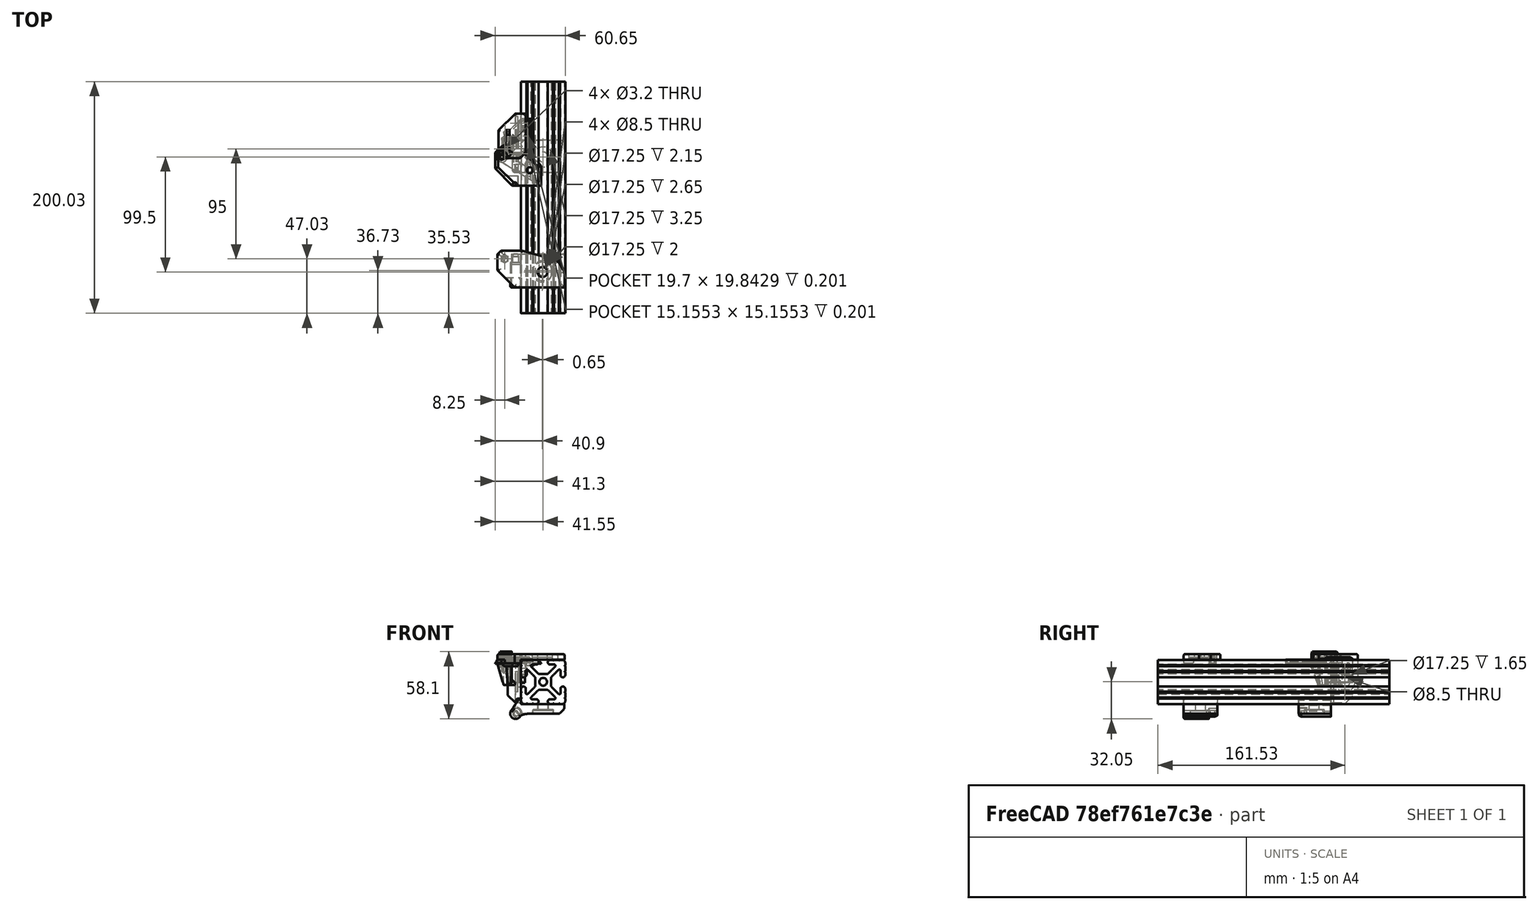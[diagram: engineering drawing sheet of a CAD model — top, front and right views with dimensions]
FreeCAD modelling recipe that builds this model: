
FCSTD DOCUMENT  (FreeCAD 0.18R)
Label: rambo-mounts
License: All rights reserved
LicenseURL: http://en.wikipedia.org/wiki/All_rights_reserved
objects: Sketcher::SketchObject×24, PartDesign::Fillet×15, PartDesign::Pad×11, PartDesign::Pocket×11, Part::Feature×6, PartDesign::Body×4, Mesh::Feature×2, PartDesign::Revolution×2, PartDesign::Chamfer×1
note: 98 computed .brp shape members not serialized (recipe doc carries the construction recipe); baked Part::Feature solids carry a one-line shape summary decoded from their .brp

FEATURE [Sketcher::SketchObject] Sketch
  MapMode = 5
  Support = -> [XY_Plane]
  sketch-geometry (7):
    g0: LineSegment StartX=-3 StartY=23 StartZ=0 EndX=-3 EndY=4.25 EndZ=0
    g1: LineSegment StartX=-3 StartY=4.25 StartZ=0 EndX=2.25 EndY=-1 EndZ=0
    g2: LineSegment StartX=2.25 StartY=-1 StartZ=0 EndX=15.7 EndY=-1 EndZ=0
    g3: LineSegment StartX=15.7 StartY=-1 StartZ=0 EndX=20.5 EndY=3.8 EndZ=0
    g4: LineSegment StartX=20.5 StartY=37.5 StartZ=0 EndX=20.5 EndY=3.8 EndZ=0
    g5: LineSegment StartX=11.5 StartY=37.5 StartZ=0 EndX=20.5 EndY=37.5 EndZ=0
    g6: LineSegment StartX=11.5 StartY=37.5 StartZ=0 EndX=-3 EndY=23 EndZ=0
  constraints (21):
    c: Coincident(g1,g0)
    c: Coincident(g2,g1)
    c: Horizontal(g2)
    c: Coincident(g4,g3)
    c: Vertical(g4)
    c: Coincident(g5,g4)
    c: Horizontal(g5)
    c: Coincident(g6,g5)
    c: Coincident(g6,g0)
    c: Angle(g1,g0) = 2.35619
    c: Angle(g0,g6) = 2.35619
    c: Angle(g3,g2) = 2.35619
    c: DistanceX(g-1,g5) = 11.5
    c: DistanceY(g-1,g5) = 37.5
    c: DistanceX(g5,g5) = 9
    c: Coincident(g3,g2)
    c: DistanceX(g-1,g2) = 15.7
    c: DistanceX(g-1,g1) = 2.25
    c: Vertical(g0)
    c: DistanceX(g0,g-1) = 3
    c: DistanceY(g1,g-1) = 1
FEATURE [Part::Feature] rambo_base_upper_mount
  shape: bbox 25.4 x 33.05 x 22.5 mm, 98 faces (baked)
  expr: Placement.Base.z = 0
FEATURE [Part::Feature] rambo_base_lower_mount
  shape: bbox 39.91 x 31.71 x 6.307 mm, 79 faces (baked)
FEATURE [Part::Feature] rambo_lid_lower_hinge
  shape: bbox 15.91 x 28.51 x 29.3 mm, 59 faces (baked)
FEATURE [Part::Feature] rambo_base_upper_mount_cs
  shape: bbox 20 x 29.18 x 3e-07 mm, 0 faces, 0 solids (baked)
FEATURE [PartDesign::Pad] Pad
  Length = 5
  Length2 = 100
  Profile = -> Sketch
  Type = 0
FEATURE [Sketcher::SketchObject] Sketch001
  AttachmentOffset = pos=(0,0,-14.5) rot=(0,0,1;0rad)
  MapMode = 5
  Placement = pos=(0,14.5,3.2e-15) rot=(1,0,0;1.5708rad)
  Support = -> [XZ_Plane]
  sketch-geometry (5):
    g0: LineSegment StartX=5 StartY=0 StartZ=0 EndX=5 EndY=-30.5 EndZ=0
    g1: LineSegment StartX=5 StartY=-30.5 StartZ=0 EndX=11.5 EndY=-37 EndZ=0
    g2: LineSegment StartX=11.5 StartY=-37 StartZ=0 EndX=16.5 EndY=-37 EndZ=0
    g3: LineSegment StartX=16.5 StartY=-37 StartZ=0 EndX=16.5 EndY=0 EndZ=0
    g4: LineSegment StartX=16.5 StartY=0 StartZ=0 EndX=5 EndY=0 EndZ=0
  constraints (15):
    c: Horizontal(g2)
    c: PointOnObject(g3,g-1)
    c: Vertical(g3)
    c: Angle(g1,g0) = 2.35619
    c: Coincident(g1,g2)
    c: Coincident(g0,g1)
    c: Coincident(g3,g2)
    c: Coincident(g4,g3)
    c: Vertical(g0)
    c: Coincident(g4,g0)
    c: Horizontal(g4)
    c: DistanceX(g-1,g0) = 5
    c: DistanceX(g-1,g3) = 16.5
    c: DistanceY(g2,g-1) = 37
    c: DistanceX(g2,g2) = 5
FEATURE [PartDesign::Pad] Pad001
  BaseFeature = -> Pad
  Length = 2
  Length2 = 100
  Profile = -> Sketch001
  Reversed = true
  Type = 0
FEATURE [Sketcher::SketchObject] Sketch002
  AttachmentOffset = pos=(0,0,16.5) rot=(0,0,1;0rad)
  MapMode = 5
  Placement = pos=(16.5,-3.7e-15,3.7e-15) rot=(0.57735,0.57735,0.57735;2.0944rad)
  Support = -> [YZ_Plane]
  sketch-geometry (6):
    g0: LineSegment StartX=16.5 StartY=0 StartZ=0 EndX=37.5 EndY=0 EndZ=0
    g1: LineSegment StartX=16.5 StartY=0 StartZ=0 EndX=16.5 EndY=-37 EndZ=0
    g2: LineSegment StartX=16.5 StartY=-37 StartZ=0 EndX=27.5 EndY=-37 EndZ=0
    g3: LineSegment StartX=37.5 StartY=0 StartZ=0 EndX=37.5 EndY=-27 EndZ=0
    g4: Circle CenterX=26.5 CenterY=-19.05 CenterZ=0 NormalX=0 NormalY=0 NormalZ=1 AngleXU=0 Radius=4.25
    g5: LineSegment StartX=27.5 StartY=-37 StartZ=0 EndX=37.5 EndY=-27 EndZ=0
  constraints (18):
    c: Coincident(g1,g0)
    c: Vertical(g1)
    c: Horizontal(g2)
    c: DistanceX(g-1,g0) = 16.5
    c: DistanceY(g2,g-1) = 37
    c: Coincident(g2,g1)
    c: Vertical(g3)
    c: Diameter(g4) = 8.5
    c: DistanceY(g4,g-1) = 19.05
    c: Horizontal(g0)
    c: DistanceY(g-1,g0) = 0
    c: DistanceX(g0,g4) = 10
    c: DistanceX(g0,g3) = 21
    c: Coincident(g5,g2)
    c: DistanceX(g2,g5) = 10
    c: Coincident(g5,g3)
    c: Angle(g3,g5) = 2.35619
    c: Coincident(g3,g0)
FEATURE [PartDesign::Pad] Pad002
  BaseFeature = -> Pad001
  Length = 5
  Length2 = 100
  Profile = -> Sketch002
  Reversed = true
  Type = 0
FEATURE [Sketcher::SketchObject] Sketch003
  AttachmentOffset = pos=(0,0,11.5) rot=(0,0,1;0rad)
  MapMode = 5
  Placement = pos=(11.5,-2.6e-15,2.6e-15) rot=(0.57735,0.57735,0.57735;2.0944rad)
  Support = -> [YZ_Plane]
  sketch-geometry (1):
    g0: Circle CenterX=26.5 CenterY=-19.05 CenterZ=0 NormalX=0 NormalY=0 NormalZ=1 AngleXU=0 Radius=8.625
  constraints (3):
    c: Diameter(g0) = 17.25
    c: DistanceY(g0,g-1) = 19.05
    c: DistanceX(g-1,g0) = 26.5
FEATURE [PartDesign::Pocket] Pocket
  BaseFeature = -> Pad002
  Length = 2
  Length2 = 100
  Profile = -> Sketch003
  Reversed = true
  Type = 0
FEATURE [Sketcher::SketchObject] Sketch004
  AttachmentOffset = pos=(2.25,7,0) rot=(0,0,1;0rad)
  MapMode = 5
  Placement = pos=(2.25,7,0) rot=(0,0,1;0rad)
  Support = -> [XY_Plane]
  sketch-geometry (8):
    g0: LineSegment StartX=0 StartY=-3.15 StartZ=0 EndX=2.72798 EndY=-1.575 EndZ=0
    g1: LineSegment StartX=2.72798 StartY=-1.575 StartZ=0 EndX=2.72798 EndY=1.575 EndZ=0
    g2: LineSegment StartX=2.72798 StartY=1.575 StartZ=0 EndX=0 EndY=3.15 EndZ=0
    g3: LineSegment StartX=0 StartY=3.15 StartZ=0 EndX=-2.72798 EndY=1.575 EndZ=0
    g4: LineSegment StartX=-2.72798 StartY=1.575 StartZ=0 EndX=-2.72798 EndY=-1.575 EndZ=0
    g5: LineSegment StartX=-2.72798 StartY=-1.575 StartZ=0 EndX=0 EndY=-3.15 EndZ=0
    g6: Circle [constr] CenterX=0 CenterY=0 CenterZ=0 NormalX=0 NormalY=0 NormalZ=1 AngleXU=0 Radius=3.15
    g7: Circle CenterX=0 CenterY=0 CenterZ=0 NormalX=0 NormalY=0 NormalZ=1 AngleXU=0 Radius=1.6
  constraints (18):
    c: Coincident(g0,g1)
    c: Coincident(g1,g2)
    c: Coincident(g2,g3)
    c: Coincident(g3,g4)
    c: Coincident(g4,g5)
    c: Coincident(g5,g0)
    c: Equal(g0, g1-g5) x5
    c: PointOnObject(g0,g6)
    c: PointOnObject(g1,g6)
    c: PointOnObject(g2,g6)
    c: PointOnObject(g3,g6)
    c: PointOnObject(g4,g6)
    c: PointOnObject(g5,g6)
    c: Vertical(g1)
    c: Coincident(g6,g-1)
    c: DistanceY(g-1,g2) = 3.15
    c: Coincident(g7,g-1)
    c: Diameter(g7) = 3.2
FEATURE [PartDesign::Pad] Pad003
  BaseFeature = -> Pocket
  Length = 3
  Length2 = 100
  Profile = -> Sketch004
  Reversed = true
  Type = 0
FEATURE [Sketcher::SketchObject] Sketch005
  AttachmentOffset = pos=(0,0,-3) rot=(0,0,1;0rad)
  MapMode = 5
  Placement = pos=(0,0,-3) rot=(0,0,1;0rad)
  Support = -> [XY_Plane]
  sketch-geometry (1):
    g0: Circle CenterX=2.25 CenterY=7 CenterZ=0 NormalX=0 NormalY=0 NormalZ=1 AngleXU=0 Radius=1.6
  constraints (3):
    c: Diameter(g0) = 3.2
    c: DistanceX(g-1,g0) = 2.25
    c: DistanceY(g-1,g0) = 7
FEATURE [PartDesign::Pocket] Pocket001
  BaseFeature = -> Pad003
  Length = 5
  Length2 = 100
  Profile = -> Sketch005
  Reversed = true
  Type = 1
FEATURE [Part::Feature] _515_extrusion_200_25mm_7_7_8in
  Placement = pos=(-110.45,65,-76.25) rot=(1,0,0;1.5708rad)
  shape: bbox 38.1 x 200 x 38.1 mm, 113 faces (baked)
FEATURE [Mesh::Feature] Einsy_base  label="Einsy-base"
  Placement = pos=(16.25,14.5,0) rot=(-0.707107,0.707107,0;3.14159rad)
FEATURE [Part::Feature] rambo_lower_mount
  Placement = pos=(2.25,-88,0) rot=(0,0,1;0rad)
  shape: bbox 58.05 x 31.7 x 8 mm, 46 faces (baked)
FEATURE [Mesh::Feature] Einsy_doors  label="Einsy-doors"
  Placement = pos=(-75.75,14.5,-51) rot=(0,0,1;4.71239rad)
FEATURE [Sketcher::SketchObject] Sketch006
  MapMode = 5
  Support = -> [XY_Plane001]
  sketch-geometry (10):
    g0: LineSegment StartX=0.5 StartY=0.25 StartZ=0 EndX=37.5 EndY=0.25 EndZ=0
    g1: LineSegment StartX=37.5 StartY=0.25 StartZ=0 EndX=37.5 EndY=4.25 EndZ=0
    g2: LineSegment StartX=33.5 StartY=8.5 StartZ=0 EndX=37.5 EndY=4.25 EndZ=0
    g3: LineSegment StartX=-8.36135 StartY=6 StartZ=0 EndX=-1.5 EndY=-4.23326 EndZ=0
    g4: LineSegment StartX=-1 StartY=-4.5 StartZ=0 EndX=0.25 EndY=-4.5 EndZ=0
    g5: LineSegment StartX=33.5 StartY=8.5 StartZ=0 EndX=0.1 EndY=8.5 EndZ=0
    g6: LineSegment StartX=0.25 StartY=-4.5 StartZ=0 EndX=0.25 EndY=0 EndZ=0
    g7: ArcOfCircle CenterX=0.5 CenterY=0 CenterZ=0 NormalX=0 NormalY=0 NormalZ=1 AngleXU=0 Radius=0.25 StartAngle=1.5708 EndAngle=3.14159
    g8: ArcOfCircle CenterX=-4.5 CenterY=8.5 CenterZ=0 NormalX=0 NormalY=0 NormalZ=1 AngleXU=0 Radius=4.6 StartAngle=3.71617 EndAngle=6.28319
    g9: ArcOfCircle CenterX=-1 CenterY=-3.89801 CenterZ=0 NormalX=0 NormalY=0 NormalZ=1 AngleXU=0 Radius=0.601989 StartAngle=3.73224 EndAngle=4.71239
  constraints (29):
    c: Horizontal(g0)
    c: Coincident(g1,g0)
    c: Vertical(g1)
    c: DistanceY(g0,g1) = 4
    c: Coincident(g2,g1)
    c: Horizontal(g5)
    c: Coincident(g5,g2)
    c: DistanceX(g2,g1) = 4
    c: Horizontal(g4)
    c: DistanceX(g-1,g4) = 0.25
    c: Coincident(g6,g4)
    c: Vertical(g6)
    c: Tangent(g0,g7) = 1.5708
    c: Tangent(g6,g7) = 1.5708
    c: DistanceX(g6,g7) = 0.25
    c: PointOnObject(g7,g-1)
    c: Diameter(g8) = 9.2
    c: DistanceX(g8,g-1) = 4.5
    c: DistanceY(g-1,g8) = 8.5
    c: DistanceX(g0,g0) = 37
    c: DistanceY(g6,g6) = 4.5
    c: Tangent(g3,g9) = -1.5708
    c: Tangent(g4,g9) = -1.5708
    c: DistanceX(g3,g9) = 0.5
    c: DistanceX(g4,g4) = 1.25
    c: Coincident(g8,g3)
    c: Coincident(g8,g5)
    c: DistanceY(g-1,g3) = 6
    c: DistanceY(g-1,g5) = 8.5
FEATURE [PartDesign::Pad] Pad004
  Length = 29
  Length2 = 100
  Profile = -> Sketch006
  Reversed = true
  Type = 0
FEATURE [Sketcher::SketchObject] Sketch007
  AttachmentOffset = pos=(-4.5,-9.3,-8.49) rot=(0,1,0;-4.71239rad)
  MapMode = 5
  Placement = pos=(-4.5,8.49,-9.3) rot=(0.57735,0.57735,0.57735;2.0944rad)
  Support = -> [XZ_Plane001]
  sketch-geometry (8):
    g0: LineSegment StartX=-1.75 StartY=9.3 StartZ=0 EndX=0 EndY=9.3 EndZ=0
    g1: LineSegment StartX=-1.75 StartY=9.3 StartZ=0 EndX=-2.5 EndY=7.15 EndZ=0
    g2: LineSegment StartX=-2.5 StartY=7.15 StartZ=0 EndX=-2.5 EndY=2 EndZ=0
    g3: LineSegment StartX=0 StartY=0 StartZ=0 EndX=0 EndY=9.3 EndZ=0
    g4: LineSegment StartX=-2.5 StartY=2 StartZ=0 EndX=-4.6 EndY=2 EndZ=0
    g5: LineSegment StartX=-4.6 StartY=2 StartZ=0 EndX=-4.6 EndY=0 EndZ=0
    g6: LineSegment StartX=-4.6 StartY=0 StartZ=0 EndX=0 EndY=0 EndZ=0
    g7: LineSegment StartX=0 StartY=9.3 StartZ=0 EndX=0 EndY=0 EndZ=0
  constraints (23):
    c: Horizontal(g0)
    c: Coincident(g2,g1)
    c: Vertical(g2)
    c: Coincident(g3,g0)
    c: Vertical(g3)
    c: Coincident(g0,g1)
    c: DistanceX(g0,g0) = 1.75
    c: PointOnObject(g3,g-2)
    c: DistanceX(g1,g3) = 2.5
    c: DistanceY(g1,g0) = 2.15
    c: DistanceY(g2,g1) = 5.15
    c: Coincident(g4,g2)
    c: Horizontal(g4)
    c: DistanceX(g4,g2) = 2.1
    c: Coincident(g5,g4)
    c: PointOnObject(g5,g-1)
    c: Vertical(g5)
    c: Coincident(g6,g5)
    c: Horizontal(g6)
    c: DistanceY(g5,g4) = 2
    c: Coincident(g7,g0)
    c: Coincident(g7,g6)
    c: Coincident(g3,g6)
FEATURE [PartDesign::Revolution] Revolution
  Angle = 360
  Axis = (0,-2e-16,1)
  Base = (-4.5,8.49,-9.3)
  BaseFeature = -> Pad004
  Midplane = true
  Profile = -> Sketch007
  ReferenceAxis = -> Sketch007 [V_Axis]
  Refine = true
FEATURE [Sketcher::SketchObject] Sketch008
  AttachmentOffset = pos=(0,0,-29) rot=(0,0,1;0rad)
  MapMode = 5
  Placement = pos=(0,0,-29) rot=(0,0,1;0rad)
  Support = -> [XY_Plane001]
  sketch-geometry (1):
    g0: Circle CenterX=-4.5 CenterY=8.5 CenterZ=0 NormalX=0 NormalY=0 NormalZ=1 AngleXU=0 Radius=4.6
  constraints (3):
    c: Diameter(g0) = 9.2
    c: DistanceX(g0,g-1) = 4.5
    c: DistanceY(g-1,g0) = 8.5
FEATURE [PartDesign::Pad] Pad005
  BaseFeature = -> Revolution
  Length = 19.7
  Length2 = 100
  Profile = -> Sketch008
  Type = 0
FEATURE [Sketcher::SketchObject] Sketch009
  MapMode = 5
  Support = -> [XY_Plane001]
  sketch-geometry (9):
    g0: ArcOfCircle CenterX=-4.5 CenterY=8.5 CenterZ=0 NormalX=0 NormalY=0 NormalZ=1 AngleXU=0 Radius=4.6 StartAngle=0 EndAngle=0.511093
    g1: Circle [constr] CenterX=-0.487831 CenterY=10.75 CenterZ=0 NormalX=0 NormalY=0 NormalZ=1 AngleXU=0 Radius=0.8
    g2: Circle [constr] CenterX=1.778 CenterY=8.5 CenterZ=0 NormalX=0 NormalY=0 NormalZ=1 AngleXU=0 Radius=0.8
    g3: Circle [constr] CenterX=9.875 CenterY=8.5 CenterZ=0 NormalX=0 NormalY=0 NormalZ=1 AngleXU=0 Radius=0.8
    g4: BSplineCurve PolesCount=3 KnotsCount=2 Degree=2 IsPeriodic=0
    g5: GeomPoint [constr] X=-0.487831 Y=10.75 Z=0
    g6: GeomPoint [constr] X=9.875 Y=8.5 Z=0
    g7: LineSegment StartX=0.1 StartY=8.5 StartZ=0 EndX=1.778 EndY=8.5 EndZ=0
    g8: LineSegment StartX=1.778 StartY=8.5 StartZ=0 EndX=9.875 EndY=8.5 EndZ=0
  constraints (21):
    c: Diameter(g0) = 9.2
    c: DistanceX(g0,g-1) = 4.5
    c: DistanceY(g-1,g0) = 8.5
    c: Radius(g1) = 0.8
    c: Equal(g1,g2)
    c: Equal(g1,g3)
    c: InternalAlignment(g1,g4)
    c: InternalAlignment(g2,g4)
    c: InternalAlignment(g3,g4)
    c: InternalAlignment(g5,g4)
    c: InternalAlignment(g6,g4)
    c: DistanceX(g-1,g4) = 9.875
    c: DistanceY(g4,g2) = 0
    c: Horizontal(g7)
    c: Coincident(g7,g2)
    c: Coincident(g0,g7)
    c: Coincident(g0,g4)
    c: DistanceY(g-1,g4) = 8.5
    c: DistanceY(g0,g0) = 2.25
    c: Coincident(g8,g4)
    c: Horizontal(g8)
FEATURE [PartDesign::Pad] Pad006
  BaseFeature = -> Pad005
  Length = 29
  Length2 = 100
  Profile = -> Sketch009
  Reversed = true
  Type = 0
FEATURE [Sketcher::SketchObject] Sketch010
  MapMode = 5
  Placement = pos=(0,0,0) rot=(1,0,0;1.5708rad)
  Support = -> [XZ_Plane001]
  sketch-geometry (1):
    g0: Circle CenterX=19.05 CenterY=-14.5 CenterZ=0 NormalX=0 NormalY=0 NormalZ=1 AngleXU=0 Radius=4.25
  constraints (3):
    c: Diameter(g0) = 8.5
    c: DistanceX(g-1,g0) = 19.05
    c: DistanceY(g0,g-1) = 14.5
FEATURE [PartDesign::Pocket] Pocket002
  BaseFeature = -> Pad006
  Length = 5
  Length2 = 100
  Profile = -> Sketch010
  Type = 1
FEATURE [Sketcher::SketchObject] Sketch011
  AttachmentOffset = pos=(0,0,-6) rot=(0,0,1;0rad)
  MapMode = 5
  Placement = pos=(0,6,1.3e-15) rot=(1,0,0;1.5708rad)
  Support = -> [XZ_Plane001]
  sketch-geometry (1):
    g0: Circle CenterX=19.05 CenterY=-14.5 CenterZ=0 NormalX=0 NormalY=0 NormalZ=1 AngleXU=0 Radius=8.625
  constraints (3):
    c: Diameter(g0) = 17.25
    c: DistanceX(g-1,g0) = 19.05
    c: DistanceY(g0,g-1) = 14.5
FEATURE [PartDesign::Pocket] Pocket003
  BaseFeature = -> Pocket002
  Length = 5
  Length2 = 100
  Profile = -> Sketch011
  Type = 0
FEATURE [PartDesign::Fillet] Fillet005
  Base = -> Pocket003 [Edge33,Edge58,Edge28,Edge52,Edge27,Edge26,Edge51,Edge15,Edge14,Edge16,Edge56]
  BaseFeature = -> Pocket003
  Radius = 1.3
FEATURE [PartDesign::Fillet] Fillet006
  Base = -> Fillet005 [Edge109]
  BaseFeature = -> Fillet005
  Radius = 0.35
FEATURE [PartDesign::Body] Body001  label="rambo-lower-hinge"
  Group = -> [Sketch006,Pad004,Sketch007,Revolution,Sketch008,Pad005,Sketch009,Pad006,Sketch010,Pocket002,Sketch011,Pocket003,Fillet005,Fillet006]
  Origin = -> Origin001
  Placement = pos=(16.25,-83.8,-38) rot=(-1,0,0;1.5708rad)
  Tip = -> Fillet006
FEATURE [Sketcher::SketchObject] Sketch012
  AttachmentOffset = pos=(16,14.5,-38.1) rot=(1,0,0;-1.5708rad)
  MapMode = 5
  Placement = pos=(16,14.5,-38.1) rot=(1,0,0;4.71239rad)
  Support = -> [XY_Plane002]
  sketch-geometry (11):
    g0: LineSegment StartX=0.5 StartY=0.25 StartZ=0 EndX=37.5 EndY=0.25 EndZ=0
    g1: LineSegment StartX=37.5 StartY=0.25 StartZ=0 EndX=37.5 EndY=4.25 EndZ=0
    g2: LineSegment StartX=33.5 StartY=8.5 StartZ=0 EndX=37.5 EndY=4.25 EndZ=0
    g3: LineSegment StartX=-2.71273 StartY=-4.5 StartZ=0 EndX=0.25 EndY=-4.5 EndZ=0
    g4: LineSegment StartX=33.5 StartY=8.5 StartZ=0 EndX=-1.752 EndY=8.5 EndZ=0
    g5: LineSegment StartX=0.25 StartY=-4.5 StartZ=0 EndX=0.25 EndY=0 EndZ=0
    g6: ArcOfCircle CenterX=0.5 CenterY=0 CenterZ=0 NormalX=0 NormalY=0 NormalZ=1 AngleXU=0 Radius=0.25 StartAngle=1.5708 EndAngle=3.14159
    g7: LineSegment StartX=-5.87481 StartY=6.5 StartZ=0 EndX=-4.064 EndY=1.4 EndZ=0
    g8: LineSegment StartX=-4.064 StartY=1.4 StartZ=0 EndX=-4.064 EndY=-3.14873 EndZ=0
    g9: LineSegment StartX=-4.064 StartY=-3.14873 StartZ=0 EndX=-2.71273 EndY=-4.5 EndZ=0
    g10: ArcOfCircle CenterX=-4.25 CenterY=8.4 CenterZ=0 NormalX=0 NormalY=0 NormalZ=1 AngleXU=0 Radius=2.5 StartAngle=0.0400107 EndAngle=4.00491
  constraints (28):
    c: Horizontal(g0)
    c: Coincident(g1,g0)
    c: Vertical(g1)
    c: DistanceY(g0,g1) = 4
    c: Coincident(g2,g1)
    c: Horizontal(g4)
    c: Coincident(g4,g2)
    c: DistanceX(g2,g1) = 4
    c: Horizontal(g3)
    c: Coincident(g5,g3)
    c: Vertical(g5)
    c: Tangent(g0,g6) = 1.5708
    c: Tangent(g5,g6) = 1.5708
    c: DistanceX(g5,g6) = 0.25
    c: PointOnObject(g6,g-1)
    c: DistanceX(g0,g0) = 37
    c: DistanceY(g5,g5) = 4.5
    c: Vertical(g8)
    c: Coincident(g9,g3)
    c: Coincident(g9,g8)
    c: Coincident(g8,g7)
    c: Angle(g9,g8) = 2.35619
    c: Diameter(g10) = 5
    c: DistanceX(g10,g-1) = 4.25
    c: DistanceY(g-1,g10) = 8.4
    c: DistanceY(g-1,g7) = 1.4
    c: Coincident(g10,g4)
    c: Coincident(g10,g7)
FEATURE [PartDesign::Pad] Pad007
  Length = 28
  Length2 = 100
  Profile = -> Sketch012
  Reversed = true
  Type = 0
FEATURE [Sketcher::SketchObject] Sketch013
  AttachmentOffset = pos=(0,0,6.5) rot=(0,0,1;0rad)
  MapMode = 5
  Placement = pos=(0,-6.5,-1.4e-15) rot=(1,0,0;1.5708rad)
  Support = -> [XZ_Plane002]
  sketch-geometry (1):
    g0: Circle CenterX=11.75 CenterY=-46.5 CenterZ=0 NormalX=0 NormalY=0 NormalZ=1 AngleXU=0 Radius=4.625
  constraints (3):
    c: Diameter(g0) = 9.25
    c: DistanceX(g-1,g0) = 11.75
    c: DistanceY(g0,g-1) = 46.5
FEATURE [PartDesign::Pocket] Pocket004
  BaseFeature = -> Pad007
  Length = 7
  Length2 = 100
  Profile = -> Sketch013
  Reversed = true
  Type = 0
FEATURE [Sketcher::SketchObject] Sketch014
  AttachmentOffset = pos=(-6.5,-46.5,11.75) rot=(0,0,1;0rad)
  MapMode = 5
  Placement = pos=(11.75,-6.5,-46.5) rot=(0.57735,0.57735,0.57735;2.0944rad)
  Support = -> [YZ_Plane002]
  sketch-geometry (5):
    g0: LineSegment StartX=-6.73205 StartY=1.5 StartZ=0 EndX=-6.73205 EndY=0 EndZ=0
    g1: LineSegment StartX=-5 StartY=2.5 StartZ=0 EndX=0 EndY=2.5 EndZ=0
    g2: LineSegment StartX=0 StartY=2.5 StartZ=0 EndX=0 EndY=0 EndZ=0
    g3: LineSegment StartX=-6.73205 StartY=0 StartZ=0 EndX=0 EndY=0 EndZ=0
    g4: LineSegment StartX=-6.73205 StartY=1.5 StartZ=0 EndX=-5 EndY=2.5 EndZ=0
  constraints (14):
    c: Vertical(g0)
    c: Horizontal(g1)
    c: Coincident(g2,g1)
    c: Vertical(g2)
    c: Coincident(g3,g2)
    c: Horizontal(g3)
    c: Coincident(g0,g3)
    c: DistanceY(g2,g2) = 2.5
    c: Coincident(g4,g0)
    c: Coincident(g4,g1)
    c: DistanceY(g0,g0) = 1.5
    c: DistanceX(g1,g1) = 5
    c: Angle(g0,g4) = 2.0944
    c: Coincident(g2,g-1)
FEATURE [PartDesign::Revolution] Revolution001
  Angle = 360
  Axis = (3e-16,1,-2e-16)
  Base = (11.75,-6.5,-46.5)
  BaseFeature = -> Pocket004
  Profile = -> Sketch014
  ReferenceAxis = -> Sketch014 [H_Axis]
FEATURE [Sketcher::SketchObject] Sketch015
  MapMode = 5
  Support = -> [XY_Plane002]
  sketch-geometry (1):
    g0: Circle CenterX=35.55 CenterY=0 CenterZ=0 NormalX=0 NormalY=0 NormalZ=1 AngleXU=0 Radius=4.25
  constraints (3):
    c: Diameter(g0) = 8.5
    c: PointOnObject(g0,g-1)
    c: DistanceX(g-1,g0) = 35.55
FEATURE [PartDesign::Pocket] Pocket005
  BaseFeature = -> Revolution001
  Length = 5
  Length2 = 100
  Profile = -> Sketch015
  Type = 1
FEATURE [Sketcher::SketchObject] Sketch016
  AttachmentOffset = pos=(0,0,-43) rot=(0,0,1;0rad)
  MapMode = 5
  Placement = pos=(0,0,-43) rot=(0,0,1;0rad)
  Support = -> [XY_Plane002]
  sketch-geometry (1):
    g0: Circle CenterX=35.55 CenterY=0 CenterZ=0 NormalX=0 NormalY=0 NormalZ=1 AngleXU=0 Radius=8.625
  constraints (3):
    c: Diameter(g0) = 17.25
    c: PointOnObject(g0,g-1)
    c: DistanceX(g-1,g0) = 35.55
FEATURE [PartDesign::Pocket] Pocket006
  BaseFeature = -> Pocket005
  Length = 4
  Length2 = 100
  Profile = -> Sketch016
  Type = 0
FEATURE [PartDesign::Chamfer] Chamfer
  Base = -> Pocket006 [Edge23,Edge40]
  BaseFeature = -> Pocket006
  Size = 1
FEATURE [PartDesign::Fillet] Fillet007
  Base = -> Chamfer [Edge6,Edge8,Edge10,Edge42,Edge37,Edge38,Edge29,Edge31,Edge49]
  BaseFeature = -> Chamfer
  Radius = 0.25
FEATURE [PartDesign::Fillet] Fillet008
  Base = -> Fillet007 [Edge61]
  BaseFeature = -> Fillet007
  Radius = 0.35
FEATURE [PartDesign::Body] Body002  label="rambo-upper-hinge"
  Group = -> [Sketch012,Pad007,Sketch013,Pocket004,Sketch014,Revolution001,Sketch015,Pocket005,Sketch016,Pocket006,Chamfer,Fillet007,Fillet008]
  Origin = -> Origin002
  Tip = -> Fillet008
FEATURE [Sketcher::SketchObject] Sketch017
  AttachmentOffset = pos=(0,0,5) rot=(0,0,1;0rad)
  MapMode = 5
  Placement = pos=(0,0,5) rot=(0,0,1;0rad)
  Support = -> [XY_Plane003]
  sketch-geometry (7):
    g0: LineSegment StartX=0 StartY=-3.5 StartZ=0 EndX=3.03109 EndY=-1.75 EndZ=0
    g1: LineSegment StartX=3.03109 StartY=-1.75 StartZ=0 EndX=3.03109 EndY=1.75 EndZ=0
    g2: LineSegment StartX=3.03109 StartY=1.75 StartZ=0 EndX=0 EndY=3.5 EndZ=0
    g3: LineSegment StartX=0 StartY=3.5 StartZ=0 EndX=-3.03109 EndY=1.75 EndZ=0
    g4: LineSegment StartX=-3.03109 StartY=1.75 StartZ=0 EndX=-3.03109 EndY=-1.75 EndZ=0
    g5: LineSegment StartX=-3.03109 StartY=-1.75 StartZ=0 EndX=0 EndY=-3.5 EndZ=0
    g6: Circle [constr] CenterX=0 CenterY=0 CenterZ=0 NormalX=0 NormalY=0 NormalZ=1 AngleXU=0 Radius=3.5
  constraints (16):
    c: Coincident(g0,g1)
    c: Coincident(g1,g2)
    c: Coincident(g2,g3)
    c: Coincident(g3,g4)
    c: Coincident(g4,g5)
    c: Coincident(g5,g0)
    c: Equal(g0, g1-g5) x5
    c: PointOnObject(g0,g6)
    c: PointOnObject(g1,g6)
    c: PointOnObject(g2,g6)
    c: PointOnObject(g3,g6)
    c: PointOnObject(g4,g6)
    c: PointOnObject(g5,g6)
    c: Coincident(g6,g-1)
    c: PointOnObject(g5,g-2)
    c: DistanceY(g-1,g2) = 3.5
FEATURE [Sketcher::SketchObject] Sketch018
  AttachmentOffset = pos=(0,0,-3) rot=(0,0,1;0rad)
  MapMode = 5
  Placement = pos=(0,0,-3) rot=(0,0,1;0rad)
  Support = -> [XY_Plane003]
  sketch-geometry (1):
    g0: Circle CenterX=0 CenterY=0 CenterZ=0 NormalX=0 NormalY=0 NormalZ=1 AngleXU=0 Radius=1.6
  constraints (2):
    c: Diameter(g0) = 3.2
    c: Coincident(g0,g-1)
FEATURE [Sketcher::SketchObject] Sketch019
  MapMode = 5
  Support = -> [XY_Plane003]
  sketch-geometry (9):
    g0: LineSegment StartX=-3 StartY=6.9 StartZ=0 EndX=15 EndY=6.9 EndZ=0
    g1: LineSegment StartX=15 StartY=6.9 StartZ=0 EndX=46.204 EndY=-1.4611 EndZ=0
    g2: LineSegment StartX=52 StartY=-11.5 StartZ=0 EndX=52 EndY=-24.8 EndZ=0
    g3: LineSegment StartX=52 StartY=-24.8 StartZ=0 EndX=8.85 EndY=-24.8 EndZ=0
    g4: LineSegment StartX=8.85 StartY=-24.8 StartZ=0 EndX=-6.05 EndY=-9.9 EndZ=0
    g5: LineSegment StartX=-6.05 StartY=-9.9 StartZ=0 EndX=-6.05 EndY=3.85 EndZ=0
    g6: LineSegment StartX=-6.05 StartY=3.85 StartZ=0 EndX=-3 EndY=6.9 EndZ=0
    g7: LineSegment StartX=46.204 StartY=-1.4611 StartZ=0 EndX=52 EndY=-11.5 EndZ=0
    g8: Circle CenterX=32.65 CenterY=-11.5 CenterZ=0 NormalX=0 NormalY=0 NormalZ=1 AngleXU=0 Radius=4.25
  constraints (27):
    c: Horizontal(g0)
    c: Vertical(g2)
    c: Horizontal(g3)
    c: Vertical(g5)
    c: Coincident(g6,g5)
    c: Coincident(g6,g0)
    c: Coincident(g4,g3)
    c: Coincident(g2,g3)
    c: Coincident(g7,g1)
    c: DistanceY(g-1,g0) = 6.9
    c: Angle(g3,g4) = 2.35619
    c: Coincident(g5,g4)
    c: DistanceX(g-1,g0) = 15
    c: Coincident(g7,g2)
    c: DistanceX(g0,g2) = 37
    c: Angle(g1,g7) = 2.35619
    c: Coincident(g1,g0)
    c: Angle(g7,g2) = 2.61799
    c: Angle(g6,g0) = 2.35619
    c: DistanceX(g5,g-1) = 6.05
    c: DistanceY(g3,g-1) = 24.8
    c: DistanceY(g8,g-1) = 11.5
    c: Diameter(g8) = 8.5
    c: DistanceY(g2,g8) = 0
    c: DistanceY(g4,g-1) = 9.9
    c: DistanceX(g0,g-1) = 3
    c: DistanceX(g-1,g8) = 32.65
FEATURE [Sketcher::SketchObject] Sketch020
  MapMode = 5
  Support = -> [XY_Plane003]
  sketch-geometry (4):
    g0: LineSegment StartX=0.3 StartY=-16.25 StartZ=0 EndX=13.9 EndY=-16.25 EndZ=0
    g1: LineSegment StartX=13.9 StartY=-16.25 StartZ=0 EndX=13.9 EndY=-24.8 EndZ=0
    g2: LineSegment StartX=0.3 StartY=-16.25 StartZ=0 EndX=8.85 EndY=-24.8 EndZ=0
    g3: LineSegment StartX=8.85 StartY=-24.8 StartZ=0 EndX=13.9 EndY=-24.8 EndZ=0
  constraints (12):
    c: Horizontal(g0)
    c: Vertical(g1)
    c: Coincident(g2,g0)
    c: Coincident(g3,g2)
    c: Coincident(g3,g1)
    c: Horizontal(g3)
    c: Coincident(g0,g1)
    c: Angle(g3,g2) = 2.35619
    c: DistanceX(g-1,g0) = 0.3
    c: DistanceX(g-1,g0) = 13.9
    c: DistanceY(g1,g-1) = 24.8
    c: DistanceY(g1,g1) = 8.55
FEATURE [PartDesign::Pad] Pad010
  Length = 5
  Length2 = 100
  Profile = -> Sketch019
  Type = 0
FEATURE [PartDesign::Pad] Pad009
  BaseFeature = -> Pad010
  Length = 3
  Length2 = 100
  Profile = -> Sketch020
  Reversed = true
  Type = 0
FEATURE [Sketcher::SketchObject] Sketch021
  AttachmentOffset = pos=(0,0,5) rot=(0,0,1;0rad)
  MapMode = 5
  Placement = pos=(0,0,5) rot=(0,0,1;0rad)
  Support = -> [XY_Plane003]
  sketch-geometry (1):
    g0: Circle CenterX=32.65 CenterY=-11.5 CenterZ=0 NormalX=0 NormalY=0 NormalZ=1 AngleXU=0 Radius=8.625
  constraints (3):
    c: DistanceX(g-1,g0) = 32.65
    c: DistanceY(g0,g-1) = 11.5
    c: Diameter(g0) = 17.25
FEATURE [PartDesign::Pocket] Pocket008
  BaseFeature = -> Pad009
  Length = 3
  Length2 = 100
  Profile = -> Sketch021
  Type = 0
FEATURE [PartDesign::Pocket] Pocket009
  BaseFeature = -> Pocket008
  Length = 3
  Length2 = 100
  Profile = -> Sketch017
  Type = 0
FEATURE [PartDesign::Pocket] Pocket007
  BaseFeature = -> Pocket009
  Length = 6
  Length2 = 100
  Profile = -> Sketch018
  Reversed = true
  Type = 1
FEATURE [Sketcher::SketchObject] Sketch022
  MapMode = 5
  Support = -> [XY_Plane003]
  sketch-geometry (8):
    g0: LineSegment StartX=0 StartY=-3.15 StartZ=0 EndX=2.72798 EndY=-1.575 EndZ=0
    g1: LineSegment StartX=2.72798 StartY=-1.575 StartZ=0 EndX=2.72798 EndY=1.575 EndZ=0
    g2: LineSegment StartX=2.72798 StartY=1.575 StartZ=0 EndX=0 EndY=3.15 EndZ=0
    g3: LineSegment StartX=0 StartY=3.15 StartZ=0 EndX=-2.72798 EndY=1.575 EndZ=0
    g4: LineSegment StartX=-2.72798 StartY=1.575 StartZ=0 EndX=-2.72798 EndY=-1.575 EndZ=0
    g5: LineSegment StartX=-2.72798 StartY=-1.575 StartZ=0 EndX=0 EndY=-3.15 EndZ=0
    g6: Circle [constr] CenterX=0 CenterY=0 CenterZ=0 NormalX=0 NormalY=0 NormalZ=1 AngleXU=0 Radius=3.15
    g7: Circle CenterX=0 CenterY=0 CenterZ=0 NormalX=0 NormalY=0 NormalZ=1 AngleXU=0 Radius=1.6
  constraints (18):
    c: Coincident(g0,g1)
    c: Coincident(g1,g2)
    c: Coincident(g2,g3)
    c: Coincident(g3,g4)
    c: Coincident(g4,g5)
    c: Coincident(g5,g0)
    c: Equal(g0, g1-g5) x5
    c: PointOnObject(g0,g6)
    c: PointOnObject(g1,g6)
    c: PointOnObject(g2,g6)
    c: PointOnObject(g3,g6)
    c: PointOnObject(g4,g6)
    c: PointOnObject(g5,g6)
    c: Coincident(g6,g-1)
    c: PointOnObject(g5,g-2)
    c: DistanceY(g-1,g2) = 3.15
    c: Coincident(g7,g-1)
    c: Radius(g7) = 1.6
FEATURE [PartDesign::Pad] Pad011
  BaseFeature = -> Pocket007
  Length = 3
  Length2 = 100
  Profile = -> Sketch022
  Reversed = true
  Type = 0
FEATURE [Sketcher::SketchObject] Sketch023
  AttachmentOffset = pos=(2.25,7,5) rot=(0,0,1;0rad)
  MapMode = 5
  Placement = pos=(2.25,7,5) rot=(0,0,1;0rad)
  Support = -> [XY_Plane]
  sketch-geometry (7):
    g0: LineSegment StartX=3.03109 StartY=-1.75 StartZ=0 EndX=3.03109 EndY=1.75 EndZ=0
    g1: LineSegment StartX=3.03109 StartY=1.75 StartZ=0 EndX=4e-16 EndY=3.5 EndZ=0
    g2: LineSegment StartX=3e-16 StartY=3.5 StartZ=0 EndX=-3.03109 EndY=1.75 EndZ=0
    g3: LineSegment StartX=-3.03109 StartY=1.75 StartZ=0 EndX=-3.03109 EndY=-1.75 EndZ=0
    g4: LineSegment StartX=-3.03109 StartY=-1.75 StartZ=0 EndX=0 EndY=-3.5 EndZ=0
    g5: LineSegment StartX=0 StartY=-3.5 StartZ=0 EndX=3.03109 EndY=-1.75 EndZ=0
    g6: Circle [constr] CenterX=0 CenterY=0 CenterZ=0 NormalX=0 NormalY=0 NormalZ=1 AngleXU=0 Radius=3.5
  constraints (16):
    c: Coincident(g0,g1)
    c: Coincident(g1,g2)
    c: Coincident(g2,g3)
    c: Coincident(g3,g4)
    c: Coincident(g4,g5)
    c: Coincident(g5,g0)
    c: Equal(g0, g1-g5) x5
    c: PointOnObject(g0,g6)
    c: PointOnObject(g1,g6)
    c: PointOnObject(g2,g6)
    c: PointOnObject(g3,g6)
    c: PointOnObject(g4,g6)
    c: PointOnObject(g5,g6)
    c: DistanceY(g-1,g1) = 3.5
    c: Vertical(g3)
    c: Coincident(g6,g-1)
FEATURE [PartDesign::Pocket] Pocket010
  BaseFeature = -> Pocket001
  Length = 3
  Length2 = 100
  Profile = -> Sketch023
  Type = 0
FEATURE [PartDesign::Fillet] Fillet
  Base = -> Pocket010 [Edge33,Edge32,Edge31,Edge36,Edge35,Edge34]
  BaseFeature = -> Pocket010
  Radius = 0.35
FEATURE [PartDesign::Fillet] Fillet015
  Base = -> Fillet [Face43]
  BaseFeature = -> Fillet
  Radius = 0.25
FEATURE [PartDesign::Fillet] Fillet016
  Base = -> Fillet015 [Edge47]
  BaseFeature = -> Fillet015
  Radius = 0.35
FEATURE [PartDesign::Fillet] Fillet017
  Base = -> Fillet016 [Edge44,Edge48,Edge53,Edge57,Edge59,Edge40,Edge42]
  BaseFeature = -> Fillet016
  Radius = 1.3
FEATURE [PartDesign::Fillet] Fillet018
  Base = -> Fillet017 [Edge1,Edge4]
  BaseFeature = -> Fillet017
  Radius = 1
FEATURE [PartDesign::Fillet] Fillet019
  Base = -> Fillet018 [Edge110,Edge112]
  BaseFeature = -> Fillet018
  Radius = 1
FEATURE [PartDesign::Body] Body  label="rambo-upper-mount"
  Group = -> [Sketch,Pad,Sketch001,Pad001,Sketch002,Pad002,Sketch003,Pocket,Sketch004,Pad003,Sketch005,Pocket001,Pocket010,Sketch023,Fillet,Fillet015,Fillet016,Fillet017,Fillet018,Fillet019]
  Origin = -> Origin
  Tip = -> Fillet019
FEATURE [PartDesign::Fillet] Fillet020
  Base = -> Pad011 [Edge31,Edge32,Edge33,Edge34,Edge35,Edge36]
  BaseFeature = -> Pad011
  Radius = 0.35
FEATURE [PartDesign::Fillet] Fillet021
  Base = -> Fillet020 [Edge15]
  BaseFeature = -> Fillet020
  Radius = 0.35
FEATURE [PartDesign::Fillet] Fillet022
  Base = -> Fillet021 [Face40]
  BaseFeature = -> Fillet021
  Radius = 0.25
FEATURE [PartDesign::Fillet] Fillet023
  Base = -> Fillet022 [Face29]
  BaseFeature = -> Fillet022
  Radius = 1.3
FEATURE [PartDesign::Fillet] Fillet024
  Base = -> Fillet023 [Edge50,Edge51,Edge33,Edge42,Edge41,Edge44,Edge46,Edge48]
  BaseFeature = -> Fillet023
  Radius = 1.3
FEATURE [PartDesign::Body] Body003  label="rambo-lower-mount"
  Group = -> [Sketch019,Pad010,Sketch020,Pad009,Sketch018,Sketch021,Pocket008,Sketch017,Pocket009,Pocket007,Sketch022,Pad011,Fillet020,Fillet021,Fillet022,Fillet023,Fillet024]
  Origin = -> Origin003
  Placement = pos=(2.25,-88,0) rot=(0,0,1;0rad)
  Tip = -> Fillet024
